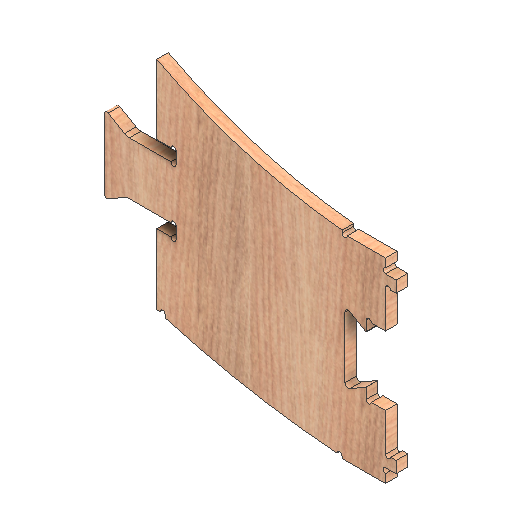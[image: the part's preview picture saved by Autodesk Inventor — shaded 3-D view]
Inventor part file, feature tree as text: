
AUTODESK INVENTOR PART (.ipt)
format: ipt  version: 2021 (Build 250183000, 183)  size: 313,856 bytes
history: native  units: mm
features: other x2, hole x1, extrude x1
ambient origin geometry x8: Origin, YZ Plane, XZ Plane, XY Plane, X Axis, Y Axis, Z Axis, Center Point
bodies: Solid1 (feature_tree)
feature tree (4):
  other  "CONTOURS"
  hole  "HOLES"  [1 undecoded]
  other  "LETTERS"
  extrude  "Extrusion4"  Depth=0.5mm
note: 1 required parameter value undecoded (feature->parameter linkage not recoverable at this tier; creation-order binding heuristic only, values carry confidence <= 0.55)
